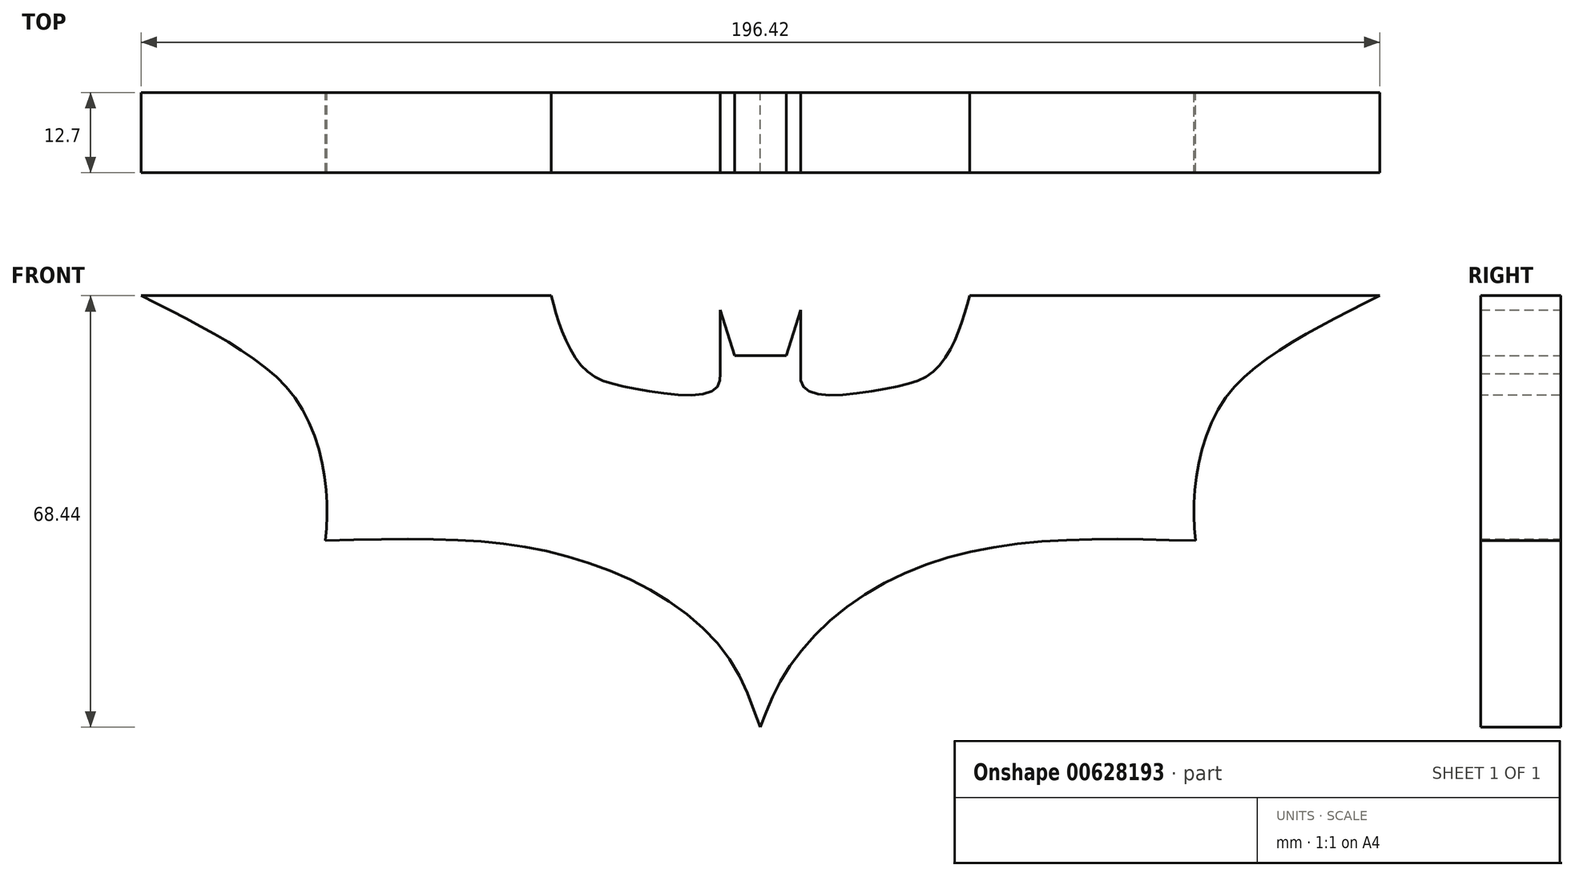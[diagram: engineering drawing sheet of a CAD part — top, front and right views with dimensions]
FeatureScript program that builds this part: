
annotation { "Feature Type Name" : "Feature", "Feature Type Description" : "" }
export const myFeature = defineFeature(function(context is Context, id is Id, definition is map)
    precondition{}
    {
        {
            var Q0;
            Q0=qCreatedBy(makeId("Front.planeOp"),FACE);
            var sketch = newSketch(context, id + "F0", { "sketchPlane" : qUnion([Q0])});
            skLineSegment(sketch, "E0", {"start": v(-98.2, 36.12) * mm, "end": v(-47.84, 36.12) * mm});
            skLineSegment(sketch, "E1", {"start": v(-47.84, 36.12) * mm, "end": v(-33.16, 36.12) * mm});
            skFitSpline(sketch, "E2", {"points": [v(-33.16, 36.12) * mm, v(-31.15, 29.79) * mm, v(-27.4, 24.03) * mm, v(-20.21, 21.44) * mm, v(-7.84, 20.87) * mm, v(-6.4, 23.74) * mm], "startDerivative": vector(8.68, -32.21) * mm, "endDerivative": vector(-3.66, 26.27) * mm});
            skLineSegment(sketch, "E3", {"start": v(-6.4, 23.74) * mm, "end": v(-6.4, 33.82) * mm});
            skLineSegment(sketch, "E4", {"start": v(-6.4, 33.82) * mm, "end": v(-4.1, 26.62) * mm});
            skFitSpline(sketch, "E5", {"points": [v(-98.2, 36.12) * mm, v(-83.24, 28.06) * mm, v(-73.46, 19.43) * mm, v(-69.14, 7.63) * mm, v(-68.99, -2.75) * mm], "startDerivative": vector(55.15, -27.62) * mm, "endDerivative": vector(-4.9, -45.44) * mm});
            skFitSpline(sketch, "E6", {"points": [v(-68.99, -2.75) * mm, v(-46.12, -2.75) * mm, v(-30.29, -5.32) * mm, v(-15.29, -11.83) * mm, v(-4.7, -21.82) * mm, v(0, -32.32) * mm], "startDerivative": vector(106, 2.93) * mm, "endDerivative": vector(23.2, -59.96) * mm});
            skLineSegment(sketch, "E7", {"start": v(-4.1, 26.62) * mm, "end": v(0, 26.62) * mm});
            skFitSpline(sketch, "E8.MirrorCS", {"points": [v(98.2, 36.12) * mm, v(83.24, 28.06) * mm, v(73.46, 19.43) * mm, v(69.14, 7.63) * mm, v(68.99, -2.75) * mm], "startDerivative": vector(-55.15, -27.62) * mm, "endDerivative": vector(4.9, -45.44) * mm});
            skLineSegment(sketch, "E9.MirrorCS", {"start": v(6.4, 33.82) * mm, "end": v(4.1, 26.62) * mm});
            skLineSegment(sketch, "E10.MirrorCS", {"start": v(47.84, 36.12) * mm, "end": v(33.16, 36.12) * mm});
            skFitSpline(sketch, "E11.MirrorCS", {"points": [v(33.16, 36.12) * mm, v(31.15, 29.79) * mm, v(27.4, 24.03) * mm, v(20.21, 21.44) * mm, v(7.84, 20.87) * mm, v(6.4, 23.74) * mm], "startDerivative": vector(-8.68, -32.21) * mm, "endDerivative": vector(3.66, 26.27) * mm});
            skLineSegment(sketch, "E12.MirrorCS", {"start": v(98.2, 36.12) * mm, "end": v(47.84, 36.12) * mm});
            skLineSegment(sketch, "E13.MirrorCS", {"start": v(6.4, 23.74) * mm, "end": v(6.4, 33.82) * mm});
            skLineSegment(sketch, "E14", {"start": v(0, 26.62) * mm, "end": v(4.1, 26.62) * mm});
            skFitSpline(sketch, "E15", {"points": [v(0, -32.32) * mm, v(3.96, -23.74) * mm, v(13.17, -13.67) * mm, v(28.14, -5.9) * mm, v(46.85, -2.73) * mm, v(68.99, -2.75) * mm], "startDerivative": vector(21.1, 55.22) * mm, "endDerivative": vector(95.44, -2.67) * mm});
            skSolve(sketch);
        }
        {
            var Q0;
            Q0 = qSketchRegion(id + "F0", true);
            extrude(context, id + "F1", {"entities" : qUnion([Q0]), "depth" : 12.7 * mm, "offsetDistance" : 25.4 * mm});
        }
    });
